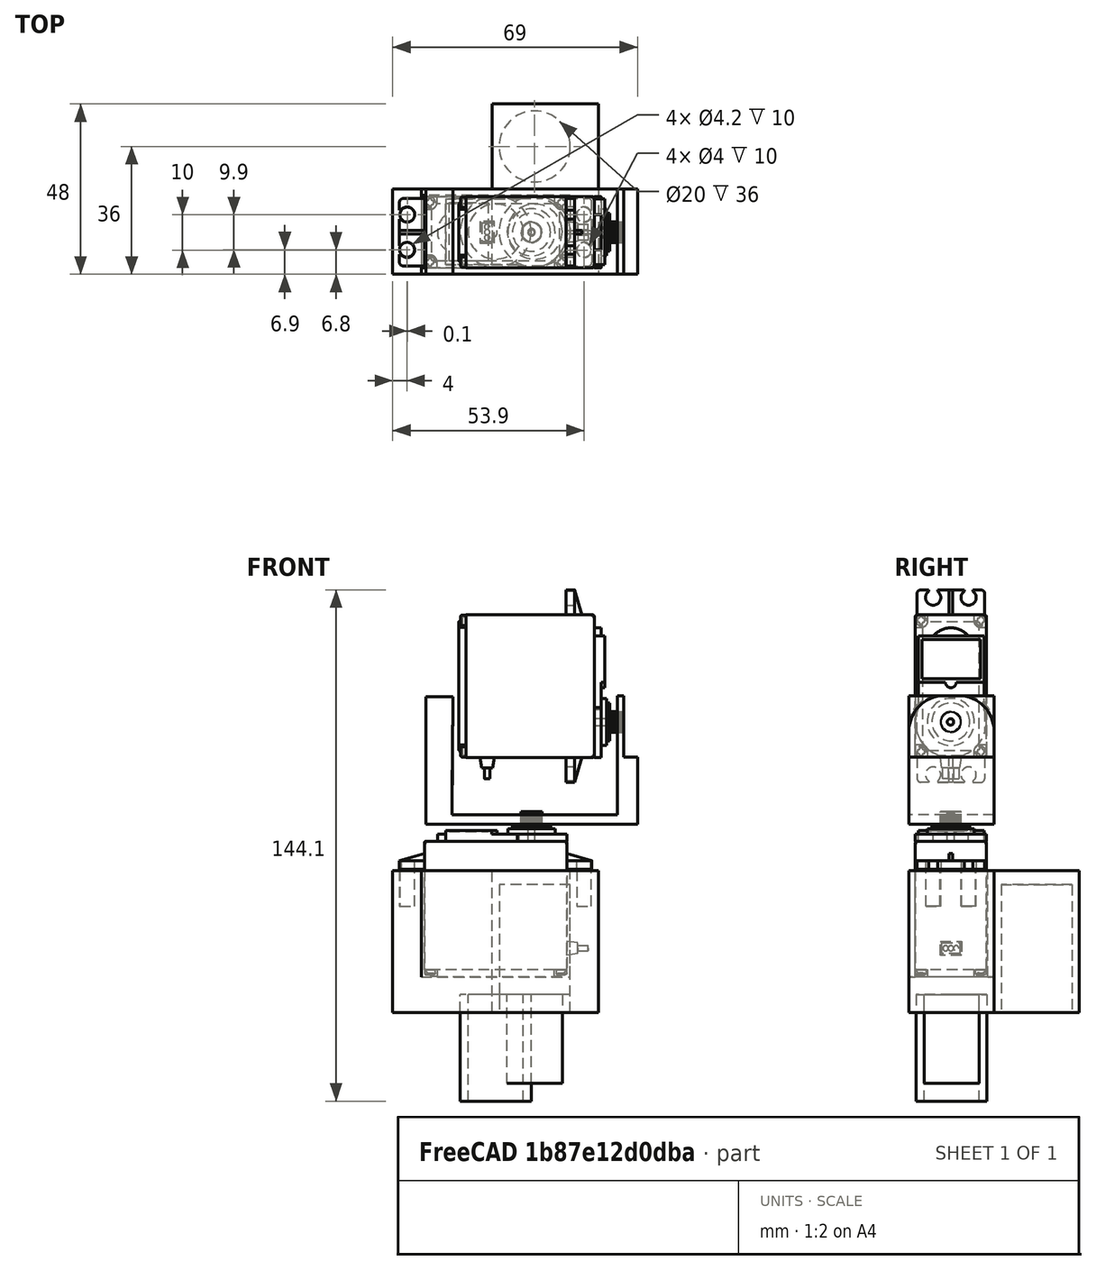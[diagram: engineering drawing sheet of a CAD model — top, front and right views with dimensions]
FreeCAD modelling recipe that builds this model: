
FCSTD DOCUMENT  (FreeCAD 0.21R33771 (Git))
Label: U_Servo_Rotativo_v1
License: All rights reserved
LicenseURL: http://en.wikipedia.org/wiki/All_rights_reserved
objects: Sketcher::SketchObject×9, PartDesign::Pad×6, PartDesign::Pocket×3, PartDesign::Body×3, Mesh::Feature×2, Part::Feature×2, Part::Fillet×2, Part::FeaturePython×1, Part::Box×1, Part::Cylinder×1, Part::Cut×1, App::DocumentObjectGroup×1
note: 38 computed .brp shape members not serialized (recipe doc carries the construction recipe); baked Part::Feature solids carry a one-line shape summary decoded from their .brp

FEATURE [Part::FeaturePython] Tube  # WARN: FeaturePython — macro-defined, semantics opaque (R4)
  AttacherType = Attacher::AttachEngine3D
  Height = 30
  InnerRadius = 7.75
  OuterRadius = 10
  Placement = pos=(0,-12,-37) rot=(0,0,1;0rad)
FEATURE [Mesh::Feature] servo_lower_cover_fake_shaft
  Placement = pos=(-6,-13,80) rot=(0,-1,0;1.5708rad)
FEATURE [Mesh::Feature] futaba  label="Servo"
  Placement = pos=(0,-3,2) rot=(0,0,1;0rad)
FEATURE [Part::Feature] Part__Feature  label="MG996R"
  Placement = pos=(0,-9,-0.5) rot=(0,0,1;0rad)
  shape: bbox 54.21 x 20.13 x 46.64 mm, 453 faces, 11 solids (baked)
FEATURE [Sketcher::SketchObject] Sketch
  FullyConstrained = false
  MapMode = 5
  Placement = pos=(0,0,0) rot=(1,0,0;1.5708rad)
  Support = -> [XZ_Plane]
  sketch-geometry (9):
    g0: LineSegment StartX=-21.001 StartY=28 StartZ=0 EndX=-29 EndY=28 EndZ=0
    g1: LineSegment StartX=-29 StartY=28 StartZ=0 EndX=-29 EndY=-2 EndZ=0
    g2: LineSegment StartX=21 StartY=28 StartZ=0 EndX=29 EndY=28 EndZ=0
    g3: LineSegment StartX=21 StartY=28 StartZ=0 EndX=21 EndY=-2 EndZ=0
    g4: LineSegment StartX=-21.001 StartY=28 StartZ=0 EndX=-21.001 EndY=-2 EndZ=0
    g5: LineSegment StartX=-29 StartY=-2 StartZ=0 EndX=-29 EndY=-12 EndZ=0
    g6: LineSegment StartX=-29 StartY=-12 StartZ=0 EndX=29 EndY=-12 EndZ=0
    g7: LineSegment StartX=29 StartY=28 StartZ=0 EndX=29 EndY=-12 EndZ=0
    g8: LineSegment StartX=-21.001 StartY=-2 StartZ=0 EndX=21 EndY=-2 EndZ=0
  constraints (18):
    c: Horizontal(g0)
    c: Coincident(g1,g0)
    c: Vertical(g1)
    c: Horizontal(g2)
    c: Coincident(g3,g2)
    c: Vertical(g3)
    c: Coincident(g4,g0)
    c: Vertical(g4)
    c: Coincident(g5,g1)
    c: Vertical(g5)
    c: Coincident(g6,g5)
    c: Horizontal(g6)
    c: Coincident(g7,g2)
    c: Coincident(g7,g6)
    c: Vertical(g7)
    c: Coincident(g8,g4)
    c: Coincident(g8,g3)
    c: Horizontal(g8)
FEATURE [PartDesign::Pad] Pad
  Direction = (0,-1,2e-16)
  Length = 24
  Length2 = 10
  Placement = pos=(0,0,0) rot=(1,0,0;1.5708rad)
  Profile = -> Sketch
  ReferenceAxis = -> Sketch [N_Axis]
  Type = 0
FEATURE [Sketcher::SketchObject] Sketch001
  FullyConstrained = false
  MapMode = 5
  Placement = pos=(0,-7.9e-15,-12) rot=(1,0,0;3.14159rad)
  Support = -> [Pad]
  sketch-geometry (1):
    g0: Circle CenterX=11 CenterY=12 CenterZ=0 NormalX=0 NormalY=0 NormalZ=1 AngleXU=0 Radius=10
FEATURE [Sketcher::SketchObject] Sketch003
  FullyConstrained = false
  MapMode = 5
  Placement = pos=(0,0,-2) rot=(0,0,1;3.14159rad)
  sketch-geometry (8):
    g0: LineSegment StartX=21 StartY=1.8 StartZ=0 EndX=21 EndY=0 EndZ=0
    g1: LineSegment StartX=-21 StartY=0 StartZ=0 EndX=-21 EndY=1.8 EndZ=0
    g2: LineSegment StartX=21 StartY=24 StartZ=0 EndX=21 EndY=22.2 EndZ=0
    g3: LineSegment StartX=-21 StartY=22.2 StartZ=0 EndX=-21 EndY=24 EndZ=0
    g4: LineSegment StartX=-21 StartY=24 StartZ=0 EndX=21 EndY=24 EndZ=0
    g5: LineSegment StartX=21 StartY=22.2 StartZ=0 EndX=-21 EndY=22.2 EndZ=0
    g6: LineSegment StartX=-21 StartY=1.8 StartZ=0 EndX=21 EndY=1.8 EndZ=0
    g7: LineSegment StartX=21 StartY=0 StartZ=0 EndX=-21 EndY=0 EndZ=0
  constraints (17):
    c: Vertical(g0)
    c: Vertical(g1)
    c: PointOnObject(g0,g-1)
    c: Vertical(g2)
    c: Vertical(g3)
    c: Coincident(g4,g3)
    c: Coincident(g4,g2)
    c: Horizontal(g4)
    c: Coincident(g5,g2)
    c: Coincident(g5,g3)
    c: Horizontal(g5)
    c: Coincident(g6,g1)
    c: Coincident(g6,g0)
    c: Horizontal(g6)
    c: Coincident(g7,g0)
    c: Coincident(g7,g1)
    c: Horizontal(g7)
FEATURE [PartDesign::Pad] Pad002
  BaseFeature = -> Pad
  Direction = (0,2e-16,1)
  Length = 30
  Length2 = 10
  Placement = pos=(0,0,0) rot=(1,0,0;1.5708rad)
  Profile = -> Sketch003
  ReferenceAxis = -> Sketch003 [N_Axis]
  Type = 0
FEATURE [PartDesign::Pocket] Pocket
  BaseFeature = -> Pad002
  Direction = (0,2e-16,1)
  Length = 5
  Length2 = 5
  Placement = pos=(0,0,0) rot=(1,0,0;1.5708rad)
  Profile = -> Sketch001
  ReferenceAxis = -> Sketch001 [N_Axis]
  Type = 0
FEATURE [Sketcher::SketchObject] Sketch004
  FullyConstrained = false
  MapMode = 5
  Placement = pos=(4e-16,-3.7e-15,-7) rot=(1,0,0;3.14159rad)
  Support = -> [Pocket]
  sketch-geometry (1):
    g0: Circle CenterX=11 CenterY=12 CenterZ=0 NormalX=0 NormalY=0 NormalZ=1 AngleXU=0 Radius=7.75
FEATURE [PartDesign::Pad] Pad003
  BaseFeature = -> Pocket
  Direction = (1e-16,-3e-16,-1)
  Length = 25
  Length2 = 10
  Placement = pos=(0,0,0) rot=(1,0,0;1.5708rad)
  Profile = -> Sketch004
  ReferenceAxis = -> Sketch004 [N_Axis]
  Type = 0
FEATURE [Sketcher::SketchObject] Sketch005
  FullyConstrained = false
  MapMode = 5
  Placement = pos=(0,1.85e-14,28) rot=(0,0,1;3.14159rad)
  Support = -> [Pad003]
  sketch-geometry (4):
    g0: Circle CenterX=-24.9 CenterY=17.2 CenterZ=0 NormalX=0 NormalY=0 NormalZ=1 AngleXU=0 Radius=2.00012
    g1: Circle CenterX=-24.9 CenterY=7.2 CenterZ=0 NormalX=0 NormalY=0 NormalZ=1 AngleXU=0 Radius=2.00121
    g2: Circle CenterX=24.9 CenterY=7.2 CenterZ=0 NormalX=0 NormalY=0 NormalZ=1 AngleXU=0 Radius=2.1
    g3: Circle CenterX=25 CenterY=17.1 CenterZ=0 NormalX=0 NormalY=0 NormalZ=1 AngleXU=0 Radius=2.10238
FEATURE [PartDesign::Pocket] Pocket001
  BaseFeature = -> Pad003
  Direction = (0,-2e-16,-1)
  Length = 10
  Length2 = 5
  Placement = pos=(0,0,0) rot=(1,0,0;1.5708rad)
  Profile = -> Sketch005
  ReferenceAxis = -> Sketch005 [N_Axis]
  Type = 0
FEATURE [PartDesign::Body] Body  label="U Servo Bracket"
  Group = -> [Sketch,Pad,Sketch001,Sketch003,Pad002,Pocket,Sketch004,Pad003,Sketch005,Pocket001]
  Origin = -> Origin
  Tip = -> Pocket001
FEATURE [Sketcher::SketchObject] Sketch006
  FullyConstrained = false
  MapMode = 5
  Placement = pos=(0,0,0) rot=(1,0,0;1.5708rad)
  Support = -> [XZ_Plane001]
  sketch-geometry (9):
    g0: LineSegment StartX=-21.001 StartY=28 StartZ=0 EndX=-29 EndY=28 EndZ=0
    g1: LineSegment StartX=-29 StartY=28 StartZ=0 EndX=-29 EndY=-2 EndZ=0
    g2: LineSegment StartX=21 StartY=28 StartZ=0 EndX=29 EndY=28 EndZ=0
    g3: LineSegment StartX=21 StartY=28 StartZ=0 EndX=21 EndY=-2 EndZ=0
    g4: LineSegment StartX=-21.001 StartY=28 StartZ=0 EndX=-21.001 EndY=-2 EndZ=0
    g5: LineSegment StartX=-29 StartY=-2 StartZ=0 EndX=-29 EndY=-12 EndZ=0
    g6: LineSegment StartX=-29 StartY=-12 StartZ=0 EndX=29 EndY=-12 EndZ=0
    g7: LineSegment StartX=29 StartY=28 StartZ=0 EndX=29 EndY=-12 EndZ=0
    g8: LineSegment StartX=-21.001 StartY=-2 StartZ=0 EndX=21 EndY=-2 EndZ=0
  constraints (18):
    c: Horizontal(g0)
    c: Coincident(g1,g0)
    c: Vertical(g1)
    c: Horizontal(g2)
    c: Coincident(g3,g2)
    c: Vertical(g3)
    c: Coincident(g4,g0)
    c: Vertical(g4)
    c: Coincident(g5,g1)
    c: Vertical(g5)
    c: Coincident(g6,g5)
    c: Horizontal(g6)
    c: Coincident(g7,g2)
    c: Coincident(g7,g6)
    c: Vertical(g7)
    c: Coincident(g8,g4)
    c: Coincident(g8,g3)
    c: Horizontal(g8)
FEATURE [PartDesign::Pad] Pad004
  Direction = (0,-1,-2e-16)
  Length = 24
  Length2 = 10
  Placement = pos=(0,0,0) rot=(1,0,0;1.5708rad)
  Profile = -> Sketch006
  ReferenceAxis = -> Sketch006 [N_Axis]
  Type = 0
FEATURE [Sketcher::SketchObject] Sketch008
  FullyConstrained = false
  MapMode = 5
  Placement = pos=(0,0,-2) rot=(0,0,1;3.14159rad)
  sketch-geometry (8):
    g0: LineSegment StartX=21 StartY=1.8 StartZ=0 EndX=21 EndY=0 EndZ=0
    g1: LineSegment StartX=-21 StartY=0 StartZ=0 EndX=-21 EndY=1.8 EndZ=0
    g2: LineSegment StartX=21 StartY=24 StartZ=0 EndX=21 EndY=22.2 EndZ=0
    g3: LineSegment StartX=-21 StartY=22.2 StartZ=0 EndX=-21 EndY=24 EndZ=0
    g4: LineSegment StartX=-21 StartY=24 StartZ=0 EndX=21 EndY=24 EndZ=0
    g5: LineSegment StartX=21 StartY=22.2 StartZ=0 EndX=-21 EndY=22.2 EndZ=0
    g6: LineSegment StartX=-21 StartY=1.8 StartZ=0 EndX=21 EndY=1.8 EndZ=0
    g7: LineSegment StartX=21 StartY=0 StartZ=0 EndX=-21 EndY=0 EndZ=0
  constraints (17):
    c: Vertical(g0)
    c: Vertical(g1)
    c: PointOnObject(g0,g-1)
    c: Vertical(g2)
    c: Vertical(g3)
    c: Coincident(g4,g3)
    c: Coincident(g4,g2)
    c: Horizontal(g4)
    c: Coincident(g5,g2)
    c: Coincident(g5,g3)
    c: Horizontal(g5)
    c: Coincident(g6,g1)
    c: Coincident(g6,g0)
    c: Horizontal(g6)
    c: Coincident(g7,g0)
    c: Coincident(g7,g1)
    c: Horizontal(g7)
FEATURE [PartDesign::Pad] Pad005
  BaseFeature = -> Pad004
  Direction = (0,0,1)
  Length = 30
  Length2 = 10
  Placement = pos=(0,0,0) rot=(1,0,0;1.5708rad)
  Profile = -> Sketch008
  ReferenceAxis = -> Sketch008 [N_Axis]
  Type = 0
FEATURE [Sketcher::SketchObject] Sketch010
  FullyConstrained = false
  MapMode = 5
  Placement = pos=(0,-6.2e-15,28) rot=(0,0,1;3.14159rad)
  sketch-geometry (4):
    g0: Circle CenterX=-24.9 CenterY=17.2 CenterZ=0 NormalX=0 NormalY=0 NormalZ=1 AngleXU=0 Radius=2.00012
    g1: Circle CenterX=-24.9 CenterY=7.2 CenterZ=0 NormalX=0 NormalY=0 NormalZ=1 AngleXU=0 Radius=2.00121
    g2: Circle CenterX=24.9 CenterY=7.2 CenterZ=0 NormalX=0 NormalY=0 NormalZ=1 AngleXU=0 Radius=2.1
    g3: Circle CenterX=25 CenterY=17.1 CenterZ=0 NormalX=0 NormalY=0 NormalZ=1 AngleXU=0 Radius=2.10238
FEATURE [PartDesign::Pocket] Pocket003
  BaseFeature = -> Pad005
  Direction = (0,2e-16,-1)
  Length = 10
  Length2 = 5
  Placement = pos=(0,0,0) rot=(1,0,0;1.5708rad)
  Profile = -> Sketch010
  ReferenceAxis = -> Sketch010 [N_Axis]
  Type = 0
FEATURE [PartDesign::Body] Body001  label="U Servo Bracket001"
  Group = -> [Sketch006,Pad004,Sketch008,Pad005,Sketch010,Pocket003]
  Origin = -> Origin001
  Tip = -> Pocket003
FEATURE [Part::Box] Box  label="Cubo"
  AttacherType = Attacher::AttachEngine3D
  Height = 40
  Length = 30
  Placement = pos=(-1,0,-12) rot=(0,0,1;0rad)
  Width = 24
FEATURE [Part::Cylinder] Cylinder  label="Cilindro"
  Angle = 360
  AttacherType = Attacher::AttachEngine3D
  FirstAngle = 0
  Height = 40
  Placement = pos=(11,12,-16) rot=(0,0,1;0rad)
  Radius = 10
  SecondAngle = 0
FEATURE [Part::Cut] Cut
  Base = -> Box
  Tool = -> Cylinder
FEATURE [App::DocumentObjectGroup] Group  label="Rotativo_abrazadera"
  Group = -> [Cut,Body001]
FEATURE [Sketcher::SketchObject] Sketch011
  FullyConstrained = false
  MapMode = 5
  Placement = pos=(0,0,0) rot=(1,0,0;1.5708rad)
  Support = -> [XZ_Plane002]
  sketch-geometry (11):
    g0: LineSegment StartX=-19.7023 StartY=41 StartZ=0 EndX=35.7664 EndY=41 EndZ=0
    g1: LineSegment StartX=-19.7023 StartY=76.9573 StartZ=0 EndX=-19.7023 EndY=41 EndZ=0
    g2: LineSegment StartX=36.0859 StartY=77.3101 StartZ=0 EndX=34.3626 EndY=77.3101 EndZ=0
    g3: LineSegment StartX=-19.7023 StartY=76.9573 StartZ=0 EndX=-12.1119 EndY=76.9573 EndZ=0
    g4: LineSegment StartX=-12.2541 StartY=43.7586 StartZ=0 EndX=34.3626 EndY=43.7586 EndZ=0
    g5: LineSegment StartX=34.3626 StartY=77.3101 StartZ=0 EndX=34.3626 EndY=43.7586 EndZ=0
    g6: LineSegment StartX=-12.1119 StartY=76.9573 StartZ=0 EndX=-12.2541 EndY=43.7586 EndZ=0
    g7: LineSegment StartX=35.7664 StartY=41 StartZ=0 EndX=40 EndY=41 EndZ=0
    g8: LineSegment StartX=40 StartY=41 StartZ=0 EndX=40 EndY=60 EndZ=0
    g9: LineSegment StartX=40 StartY=60 StartZ=0 EndX=36.0859 EndY=60 EndZ=0
    g10: LineSegment StartX=36.0859 StartY=77.3101 StartZ=0 EndX=36.0859 EndY=60 EndZ=0
  constraints (21):
    c: Horizontal(g0)
    c: Coincident(g1,g0)
    c: Vertical(g1)
    c: Horizontal(g2)
    c: Coincident(g3,g1)
    c: Horizontal(g3)
    c: Horizontal(g4)
    c: Coincident(g5,g2)
    c: Coincident(g5,g4)
    c: Vertical(g5)
    c: Coincident(g6,g3)
    c: Coincident(g6,g4)
    c: Coincident(g7,g0)
    c: Horizontal(g7)
    c: Coincident(g8,g7)
    c: Vertical(g8)
    c: Coincident(g9,g8)
    c: Horizontal(g9)
    c: Coincident(g10,g2)
    c: Coincident(g10,g9)
    c: Vertical(g10)
FEATURE [Part::Feature] Part__Feature001  label="MG996R001"
  Placement = pos=(-9,-9,80) rot=(0,1,0;1.5708rad)
  shape: bbox 46.64 x 20.13 x 54.21 mm, 453 faces, 11 solids (baked)
FEATURE [PartDesign::Pad] Pad006
  Direction = (0,-1,2e-16)
  Length = 24
  Length2 = 10
  Placement = pos=(0,0,0) rot=(1,0,0;1.5708rad)
  Profile = -> Sketch011
  ReferenceAxis = -> Sketch011 [N_Axis]
  Type = 0
FEATURE [PartDesign::Body] Body002
  Group = -> [Sketch011,Pad006]
  Origin = -> Origin002
  Tip = -> Pad006
FEATURE [Part::Fillet] Fillet
  Base = -> Pad006
  Edges = 2 edges r=10: [Edge24,Edge25]
FEATURE [Part::Fillet] Fillet001
  Base = -> Fillet
  Edges = 2 edges r=8: [Edge19,Edge28]
